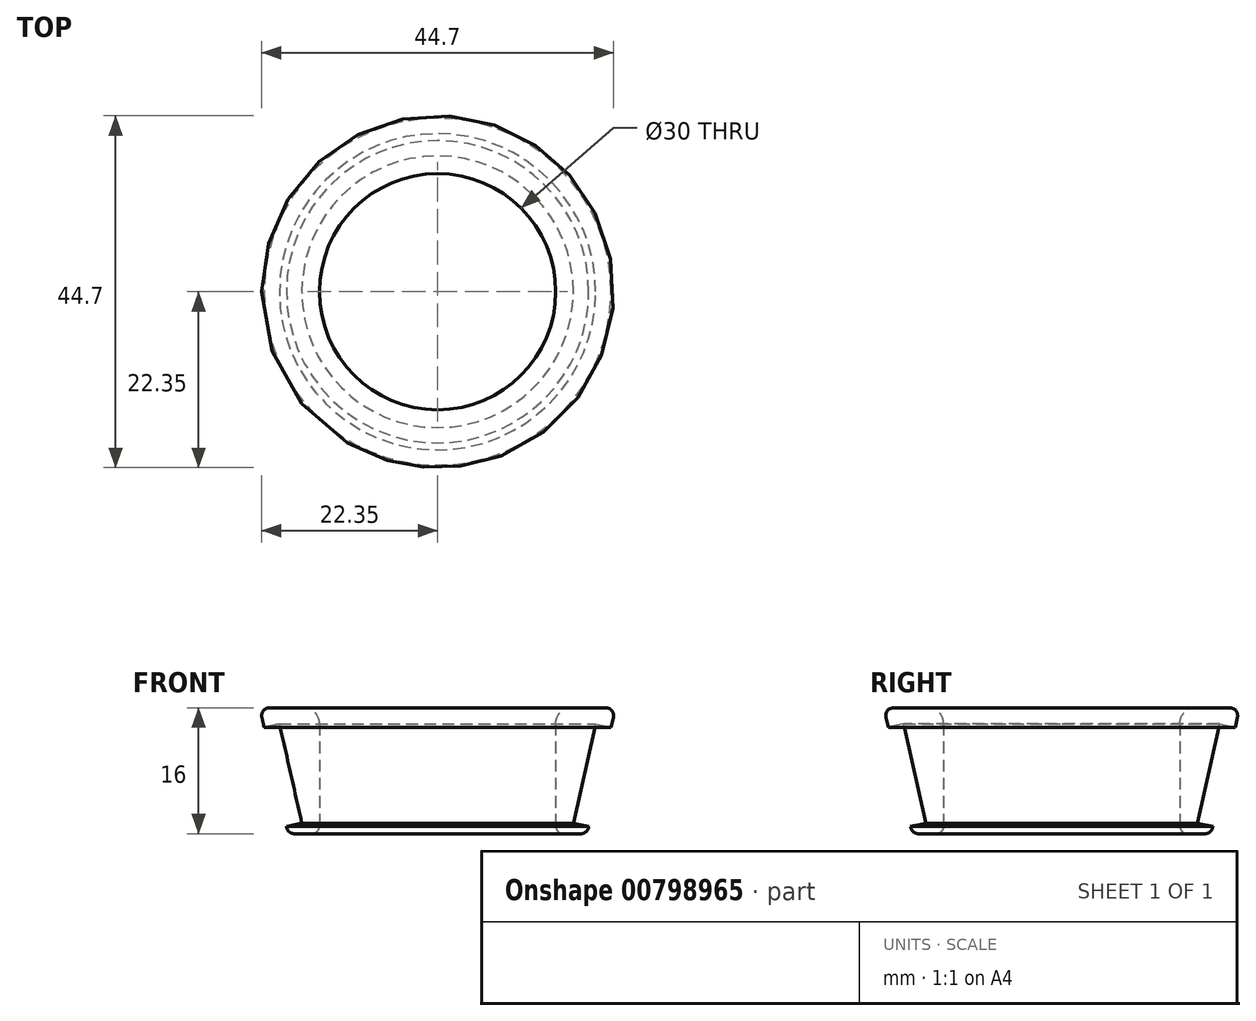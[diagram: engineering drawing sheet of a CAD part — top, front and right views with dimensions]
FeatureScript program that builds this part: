
annotation { "Feature Type Name" : "Feature", "Feature Type Description" : "" }
export const myFeature = defineFeature(function(context is Context, id is Id, definition is map)
    precondition{}
    {
        {
            var Q0;
            Q0=qCreatedBy(makeId("Front.planeOp"),FACE);
            var sketch = newSketch(context, id + "F0", { "sketchPlane" : qUnion([Q0])});
            skLineSegment(sketch, "E0", {"start": v(0, 0) * mm, "end": v(0, 17.84) * mm, "construction": true});
            skLineSegment(sketch, "E1", {"start": v(0, 0) * mm, "end": v(-19.68, 0) * mm, "construction": true});
            skLineSegment(sketch, "E2", {"start": v(-15, 1) * mm, "end": v(-15, 14) * mm});
            skLineSegment(sketch, "E3", {"start": v(-17, 16) * mm, "end": v(-21.35, 16) * mm});
            skLineSegment(sketch, "E4", {"start": v(-22.33, 14.78) * mm, "end": v(-22.04, 13.5) * mm});
            skLineSegment(sketch, "E5", {"start": v(-22.04, 13.5) * mm, "end": v(-20.08, 13.93) * mm});
            skLineSegment(sketch, "E6", {"start": v(-20.08, 13.93) * mm, "end": v(-17.25, 1.34) * mm});
            skLineSegment(sketch, "E7", {"start": v(-17.25, 1.34) * mm, "end": v(-19.2, 0.9) * mm});
            skLineSegment(sketch, "E8", {"start": v(-18.2, 0) * mm, "end": v(-16, 0) * mm});
            skLineSegment(sketch, "E9", {"start": v(-19.2, 0.9) * mm, "end": v(-19.18, 0.78) * mm});
            skPoint(sketch, "E10.visualSharp", {"position": v(-15, 16) * mm});
            skArc(sketch, "E10.filletArc", {"start": v(-15, 14) * mm, "mid": v(-15.59, 15.41) * mm, "end": v(-17, 16) * mm});
            skPoint(sketch, "E11.visualSharp", {"position": v(-22.6, 16) * mm});
            skArc(sketch, "E11.filletArc", {"start": v(-21.35, 16) * mm, "mid": v(-22.13, 15.62) * mm, "end": v(-22.33, 14.78) * mm});
            skPoint(sketch, "E12.visualSharp", {"position": v(-19, 0) * mm});
            skArc(sketch, "E12.filletArc", {"start": v(-19.18, 0.78) * mm, "mid": v(-18.82, 0.22) * mm, "end": v(-18.2, 0) * mm});
            skPoint(sketch, "E13.visualSharp", {"position": v(-15, 0) * mm});
            skArc(sketch, "E13.filletArc", {"start": v(-16, 0) * mm, "mid": v(-15.3, 0.3) * mm, "end": v(-15, 1) * mm});
            skSolve(sketch);
        }
        {
            var Q0;
            Q0=makeQuery(id+"F0.imprint","IMPRINT",FACE,{"disambiguationData":[TD([[makeQuery(id+"F0.imprint","IMPRINT",EDGE,{"derivedFrom":sQuery(id+"F0.wireOp",EDGE,"E2")}),1.0]])]});
            var Q1;
            Q1=sQuery(id+"F0.wireOp",EDGE,"E0");
            revolve(context, id + "F1", {"surfaceOperationType" : NewSurfaceOperationType.NEW, "entities" : qUnion([Q0]), "axis" : qUnion([Q1]), "revolveType" : RevolveType.FULL});
        }
    });
